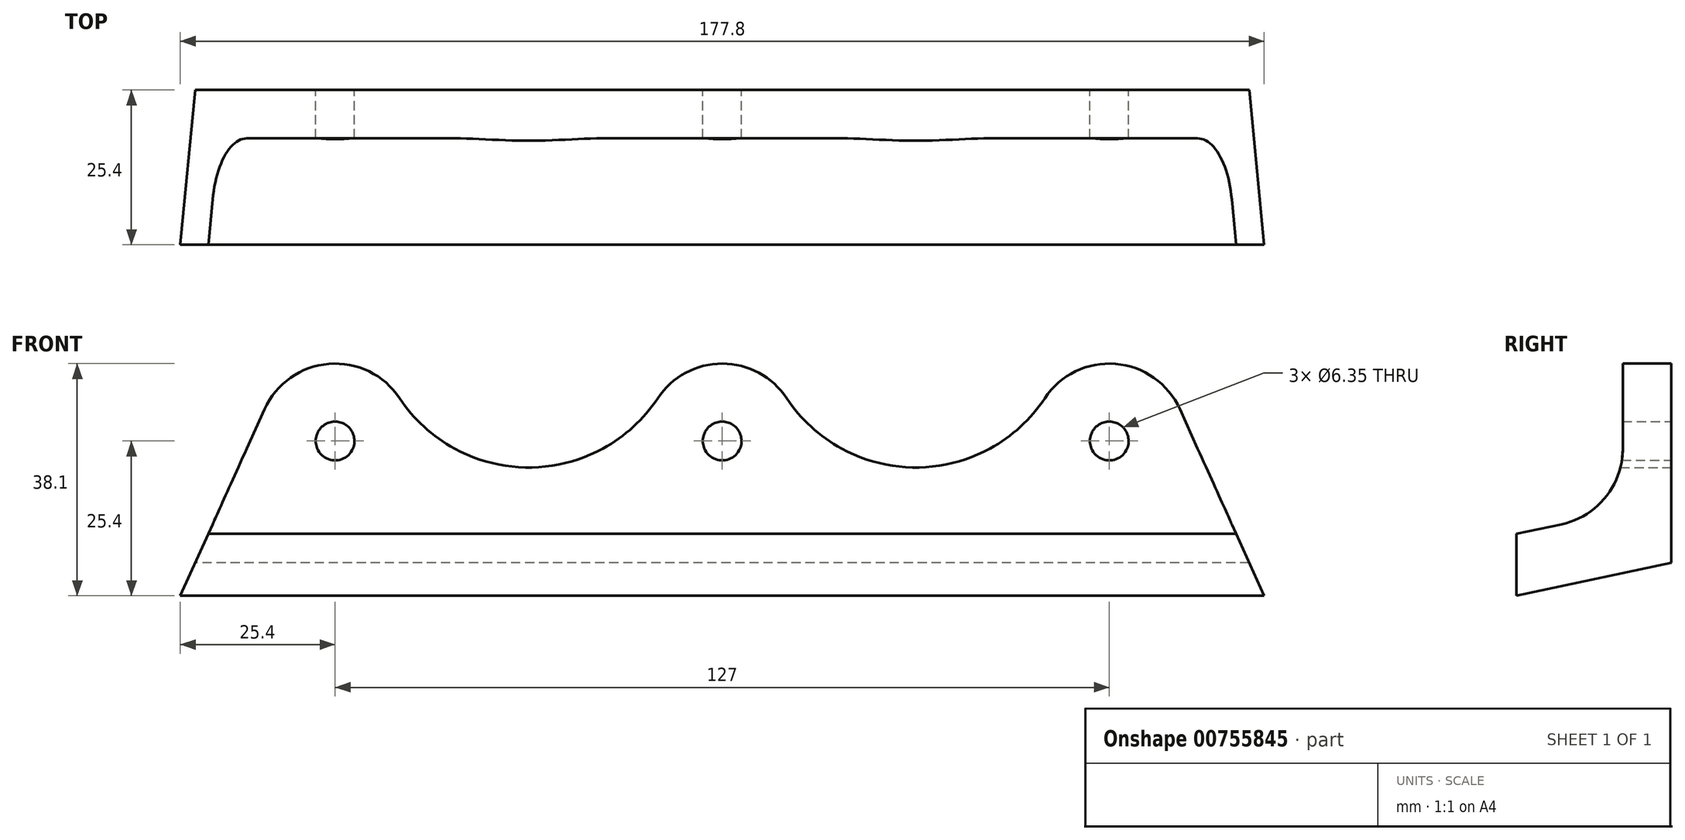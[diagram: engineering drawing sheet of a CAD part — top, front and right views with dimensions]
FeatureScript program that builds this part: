
annotation { "Feature Type Name" : "Feature", "Feature Type Description" : "" }
export const myFeature = defineFeature(function(context is Context, id is Id, definition is map)
    precondition{}
    {
        {
            var Q0;
            Q0=qCreatedBy(makeId("Front.planeOp"),FACE);
            var sketch = newSketch(context, id + "F0", { "sketchPlane" : qUnion([Q0])});
            skLineSegment(sketch, "E0.bottom", {"start": v(-88.9, 0) * mm, "end": v(88.9, 0) * mm});
            skCircle(sketch, "E1", {"center": v(-63.5, 25.4) * mm, "radius": 3.18 * mm});
            skCircle(sketch, "E2", {"center": v(63.5, 25.4) * mm, "radius": 3.18 * mm});
            skCircle(sketch, "E3", {"center": v(0, 25.4) * mm, "radius": 3.18 * mm});
            skArc(sketch, "E4", {"start": v(-52.92, 32.42) * mm, "mid": v(-64.53, 38.06) * mm, "end": v(-75.08, 30.63) * mm});
            skArc(sketch, "E5", {"start": v(10.58, 32.42) * mm, "mid": v(0, 38.1) * mm, "end": v(-10.58, 32.42) * mm});
            skArc(sketch, "E6", {"start": v(75.08, 30.63) * mm, "mid": v(64.53, 38.06) * mm, "end": v(52.92, 32.42) * mm});
            skArc(sketch, "E7", {"start": v(-52.92, 32.42) * mm, "mid": v(-31.75, 21.06) * mm, "end": v(-10.58, 32.42) * mm});
            skArc(sketch, "E8", {"start": v(10.58, 32.42) * mm, "mid": v(31.75, 21.06) * mm, "end": v(52.92, 32.42) * mm});
            skLineSegment(sketch, "E9", {"start": v(-88.9, 0) * mm, "end": v(-75.08, 30.63) * mm});
            skLineSegment(sketch, "E10", {"start": v(88.9, 0) * mm, "end": v(75.08, 30.63) * mm});
            skSolve(sketch);
        }
        {
            var Q0;
            Q0 = qSketchRegion(id + "F0", true);
            extrude(context, id + "F1", {"entities" : qUnion([Q0]), "depth" : 25.4 * mm, "offsetDistance" : 25.4 * mm});
        }
        {
            var Q0;
            Q0=qCreatedBy(makeId("Right.planeOp"),FACE);
            var sketch = newSketch(context, id + "F2", { "sketchPlane" : qUnion([Q0])});
            skLineSegment(sketch, "E11.top", {"start": v(0, 38.1) * mm, "end": v(-7.92, 38.1) * mm});
            skLineSegment(sketch, "E11.left", {"start": v(0, 5.4) * mm, "end": v(0, 38.1) * mm});
            skLineSegment(sketch, "E11.right", {"start": v(-25.4, 0) * mm, "end": v(-25.4, 10.16) * mm});
            skLineSegment(sketch, "E12", {"start": v(-25.4, 0) * mm, "end": v(0, 5.4) * mm});
            skLineSegment(sketch, "E13.bottom", {"start": v(6.72, -3.06) * mm, "end": v(-32.23, -3.06) * mm});
            skLineSegment(sketch, "E13.top", {"start": v(6.72, 42.74) * mm, "end": v(-32.23, 42.74) * mm});
            skLineSegment(sketch, "E13.left", {"start": v(6.72, -3.06) * mm, "end": v(6.72, 42.74) * mm});
            skLineSegment(sketch, "E13.right", {"start": v(-32.23, -3.06) * mm, "end": v(-32.23, 42.74) * mm});
            skLineSegment(sketch, "E14", {"start": v(-7.92, 38.1) * mm, "end": v(-7.92, 24.16) * mm});
            skLineSegment(sketch, "E15", {"start": v(-25.4, 10.16) * mm, "end": v(-17.98, 11.74) * mm});
            skPoint(sketch, "E16.visualSharp", {"position": v(-7.92, 13.87) * mm});
            skArc(sketch, "E16.filletArc", {"start": v(-17.98, 11.74) * mm, "mid": v(-10.76, 16.17) * mm, "end": v(-7.92, 24.16) * mm});
            skSolve(sketch);
        }
        {
            var Q0;
            Q0=makeQuery(id+"F2.imprint","IMPRINT",FACE,{"disambiguationData":[TD([[makeQuery(id+"F2.imprint","IMPRINT",EDGE,{"derivedFrom":sQuery(id+"F2.wireOp",EDGE,"E11.top")}),-1.0]])]});
            extrude(context, id + "F3", {"entities" : qUnion([Q0]), "operationType" : NewBodyOperationType.REMOVE, "endBound" : BoundingType.SYMMETRIC, "depth" : 381 * mm, "offsetDistance" : 25.4 * mm});
        }
    });
